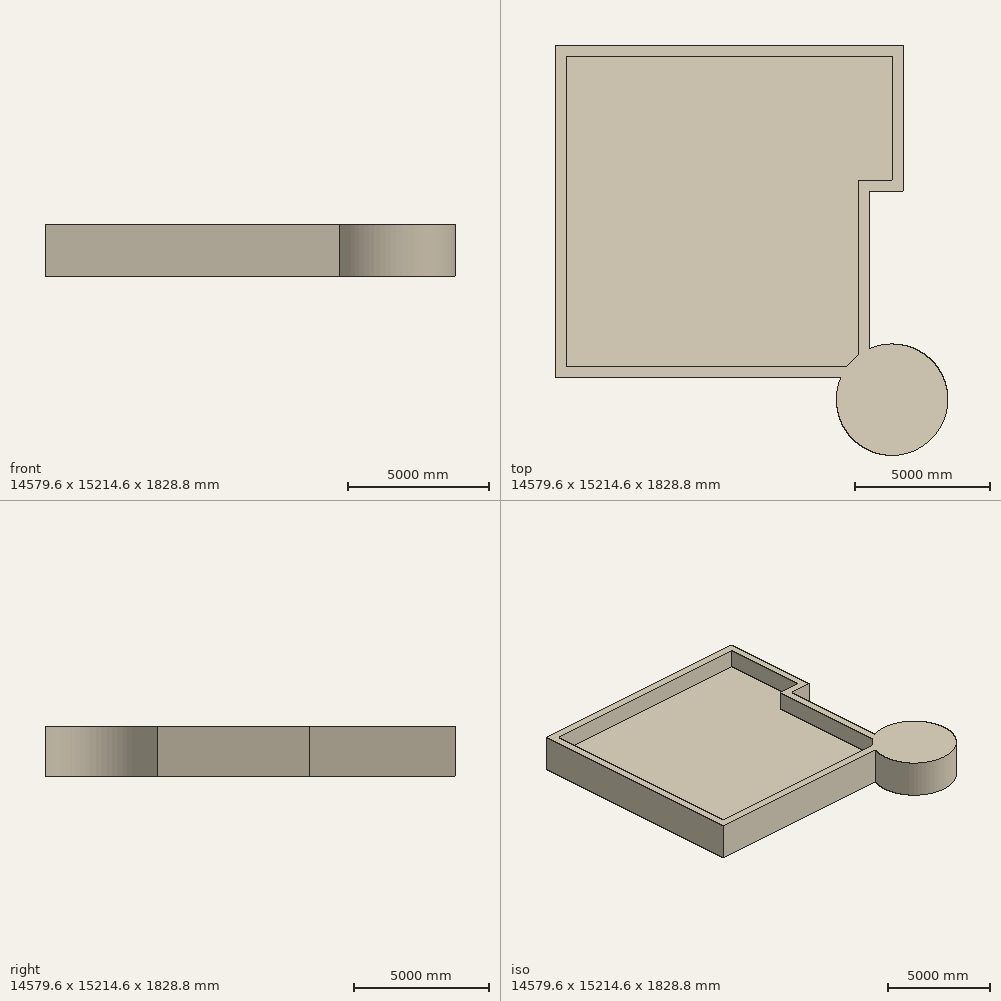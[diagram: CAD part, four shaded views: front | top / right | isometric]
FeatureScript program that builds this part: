
annotation { "Feature Type Name" : "Feature", "Feature Type Description" : "" }
export const myFeature = defineFeature(function(context is Context, id is Id, definition is map)
    precondition{}
    {
        {
            var Q0;
            Q0=qCreatedBy(makeId("Top.planeOp"),FACE);
            var sketch = newSketch(context, id + "F0", { "sketchPlane" : qUnion([Q0])});
            skLineSegment(sketch, "E0.bottom", {"start": v(0, 0) * mm, "end": v(10611.12, 0) * mm});
            skLineSegment(sketch, "E0.top", {"start": v(0, 12319) * mm, "end": v(12915.9, 12319) * mm});
            skLineSegment(sketch, "E0.left", {"start": v(0, 0) * mm, "end": v(0, 12319) * mm});
            skLineSegment(sketch, "E0.right", {"start": v(12915.9, 6908.8) * mm, "end": v(12915.9, 12319) * mm});
            skArc(sketch, "E1", {"start": v(10611.12, 0) * mm, "mid": v(13973.28, -2289.28) * mm, "end": v(11684, 1072.88) * mm});
            skLineSegment(sketch, "E2.top", {"start": v(12915.9, 6908.8) * mm, "end": v(11684, 6908.8) * mm});
            skLineSegment(sketch, "E2.right", {"start": v(11684, 1072.88) * mm, "end": v(11684, 6908.8) * mm});
            skSolve(sketch);
        }
        {
            var Q0;
            Q0 = qSketchRegion(id + "F0", true);
            extrude(context, id + "F1", {"entities" : qUnion([Q0]), "depth" : 914.4 * mm, "offsetDistance" : 25.4 * mm});
        }
        {
            var Q0;
            Q0=makeQuery(id+"F1.opExtrude","CAP_FACE",FACE,{"disambiguationData":[OSD([sQuery(id+"F0.wireOp",EDGE,"E0.bottom"),sQuery(id+"F0.wireOp",EDGE,"E0.top"),sQuery(id+"F0.wireOp",EDGE,"E0.left"),sQuery(id+"F0.wireOp",EDGE,"E0.right"),sQuery(id+"F0.wireOp",EDGE,"E1"),sQuery(id+"F0.wireOp",EDGE,"E2.top"),sQuery(id+"F0.wireOp",EDGE,"E2.right")])],"isStart":false});
            var sketch = newSketch(context, id + "F2", { "sketchPlane" : qUnion([Q0])});
            skLineSegment(sketch, "E3", {"start": v(406.4, 406.4) * mm, "end": v(406.4, 11912.6) * mm});
            skLineSegment(sketch, "E4", {"start": v(406.4, 11912.6) * mm, "end": v(12509.5, 11912.6) * mm});
            skLineSegment(sketch, "E5", {"start": v(12509.5, 11912.6) * mm, "end": v(12509.5, 7315.2) * mm});
            skLineSegment(sketch, "E6", {"start": v(12509.5, 7315.2) * mm, "end": v(11277.6, 7315.2) * mm});
            skLineSegment(sketch, "E7", {"start": v(11277.6, 7315.2) * mm, "end": v(11277.6, 838.15) * mm});
            skLineSegment(sketch, "E8", {"start": v(406.4, 406.4) * mm, "end": v(10845.85, 406.4) * mm});
            skLineSegment(sketch, "E9", {"start": v(10845.85, 406.4) * mm, "end": v(11277.6, 838.15) * mm});
            skSolve(sketch);
        }
        {
            var Q0;
            Q0=makeQuery(id+"F2.imprint","IMPRINT",FACE,{"disambiguationData":[TD([[makeQuery(id+"F2.imprint","IMPRINT",EDGE,{"derivedFrom":sQuery(id+"F2.wireOp",EDGE,"E3")}),1.0]])]});
            extrude(context, id + "F3", {"entities" : qUnion([Q0]), "operationType" : NewBodyOperationType.ADD, "depth" : 914.4 * mm, "offsetDistance" : 25.4 * mm});
        }
    });
